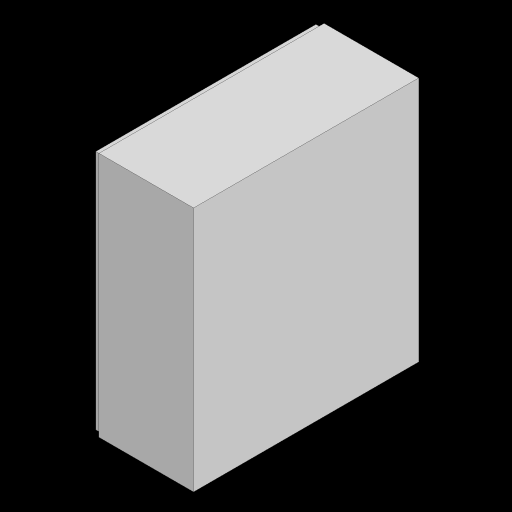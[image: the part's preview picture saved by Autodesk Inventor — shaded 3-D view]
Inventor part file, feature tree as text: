
AUTODESK INVENTOR PART (.ipt)
format: ipt  version: 2023 (Build 270158000, 158)  size: 313,344 bytes
history: native  units: in
note: dims shown in document units (in); Inventor stores cm internally (conversion verified against a paired STEP export)
features: extrude x10, sketch x10, projected_geometry x5, plane x2, fillet x2, split x1
ambient origin geometry x8: Origin, YZ Plane, XZ Plane, XY Plane, X Axis, Y Axis, Z Axis, Center Point
bodies: Solid1 (feature_tree)
feature tree (30):
  extrude  "Extrusion1"  Depth=3.937in
  sketch  "Sketch2"  dims[d2=5.1181in d3=0.0in d4=0.315in d5=0.0in]
  extrude  "Extrusion2"  Depth=0.315in TaperAngle=0.0deg
  extrude  "Extrusion3"  Depth=3.937in
  plane  "Work Plane1"
  extrude  "Extrusion4"  Depth=5.1181in
  fillet  "Fillet1"  Radius=5.1181in
  sketch  "Sketch8"  dims[d8=1.9685in d9=2.5591in d10=5.1181in]
  extrude  "Extrusion10"  Depth=0.1496in
  extrude  "Extrusion11"  [1 undecoded]
  fillet  "Fillet2"  Radius=0.1969in
  extrude  "Extrusion12"  Depth=0.1969in
  extrude  "Extrusion13"  Depth=3.5433in TaperAngle=0.0deg
  extrude  "Extrusion14"  Depth=0.1969in TaperAngle=0.0deg
  plane  "Work Plane2"
  split  "Split1"
  extrude  "Extrusion15"  Depth=0.1181in TaperAngle=0.0deg
  sketch  "Sketch1"  dims[d0=4.685in d1=3.937in]
  sketch  "Sketch3"  dims[d6=3.5433in d7=3.937in]
  projected_geometry  "Projected Loop1"
  sketch  "Sketch10"  dims[d11=2.874in d12=0.1496in]
  projected_geometry  "Projected Loop2"
  sketch  "Sketch12"  dims[d13=0.7087in d14=0.0in d15=-0.1969in d16=0.1969in]
  projected_geometry  "Projected Loop4"
  sketch  "Sketch13"  dims[d17=0.1969in d18=0.1969in]
  sketch  "Sketch14"  dims[d19=3.5433in d20=0.0in d21=3.5433in d22=0.0in]
  sketch  "Sketch15"  dims[d23=0.1969in d74=0.1969in d75=0.0in]
  sketch  "Sketch18"  dims[d82=4.685in d84=5.0in d85=0.0in d86=0.1969in d87=45.0deg d88=45.0deg d90=45.0deg d91=45.0deg d92=0.7874in d93=0.9843in d94=0.7874in d95=0.9843in d96=0.0394in d97=3.3465in d98=4.3307in d99=3.5433in d100=0.0984in d101=0.1575in d102=0.1693in d103=0.1417in d104=0.1969in d105=0.1693in d107=4.7244in d108=0.1969in d109=0.1575in d110=0.1417in d111=0.1969in d112=0.1417in d113=0.1969in d114=0.1417in d115=0.1969in d116=0.1181in d117=0.0in d118=0.7087in d119=0.1181in d121=0.7087in d122=1.3386in d123=0.7874in d124=0.0in d125=45.0deg d126=2.874in d129=3.5433in d130=0.1673in d131=0.1417in d135=0.1417in d136=0.1417in d137=0.1417in d138=1.5748in d139=0.0in d140=0.0512in d141=0.1181in d142=0.0in]
  projected_geometry  "Projected Loop5"
  projected_geometry  "Project Cut Edges1"
note: 1 required parameter value undecoded (feature->parameter linkage not recoverable at this tier; creation-order binding heuristic only, values carry confidence <= 0.55)
